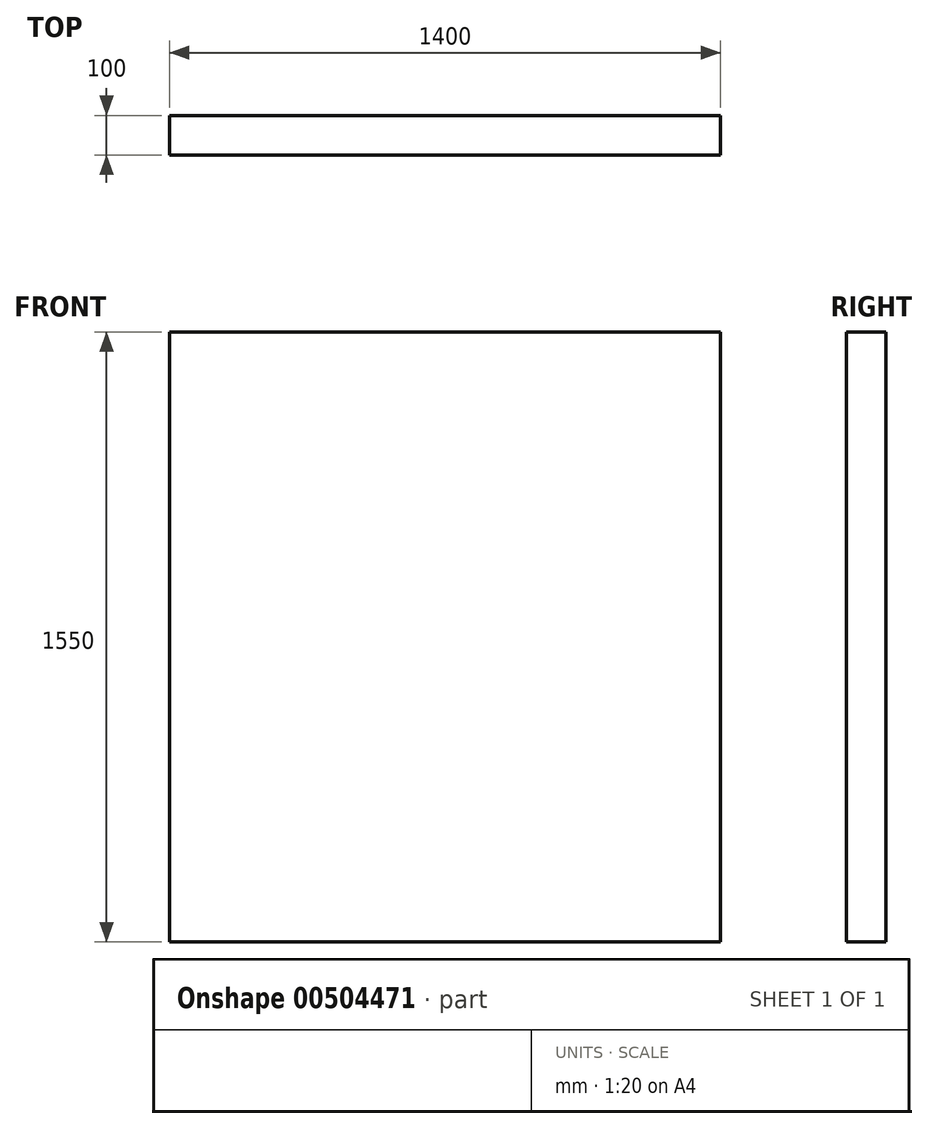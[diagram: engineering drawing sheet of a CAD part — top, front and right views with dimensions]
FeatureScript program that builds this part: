
annotation { "Feature Type Name" : "Feature", "Feature Type Description" : "" }
export const myFeature = defineFeature(function(context is Context, id is Id, definition is map)
    precondition{}
    {
        {
            var Q0;
            Q0=qCreatedBy(makeId("Top.planeOp"),FACE);
            var sketch = newSketch(context, id + "F0", { "sketchPlane" : qUnion([Q0])});
            skLineSegment(sketch, "E0.bottom", {"start": v(-700, 0) * mm, "end": v(700, 0) * mm});
            skLineSegment(sketch, "E0.top", {"start": v(-700, 100) * mm, "end": v(700, 100) * mm});
            skLineSegment(sketch, "E0.left", {"start": v(-700, 100) * mm, "end": v(-700, 0) * mm});
            skLineSegment(sketch, "E0.right", {"start": v(700, 100) * mm, "end": v(700, 0) * mm});
            skSolve(sketch);
        }
        {
            var Q0;
            Q0=makeQuery(id+"F0.imprint","IMPRINT",FACE,{"disambiguationData":[TD([[makeQuery(id+"F0.imprint","IMPRINT",EDGE,{"derivedFrom":sQuery(id+"F0.wireOp",EDGE,"E0.bottom")}),1.0]])]});
            extrude(context, id + "F1", {"entities" : qUnion([Q0]), "depth" : 850 * mm, "hasSecondDirection" : true, "secondDirectionOppositeDirection" : true, "secondDirectionDepth" : 700 * mm});
        }
    });
